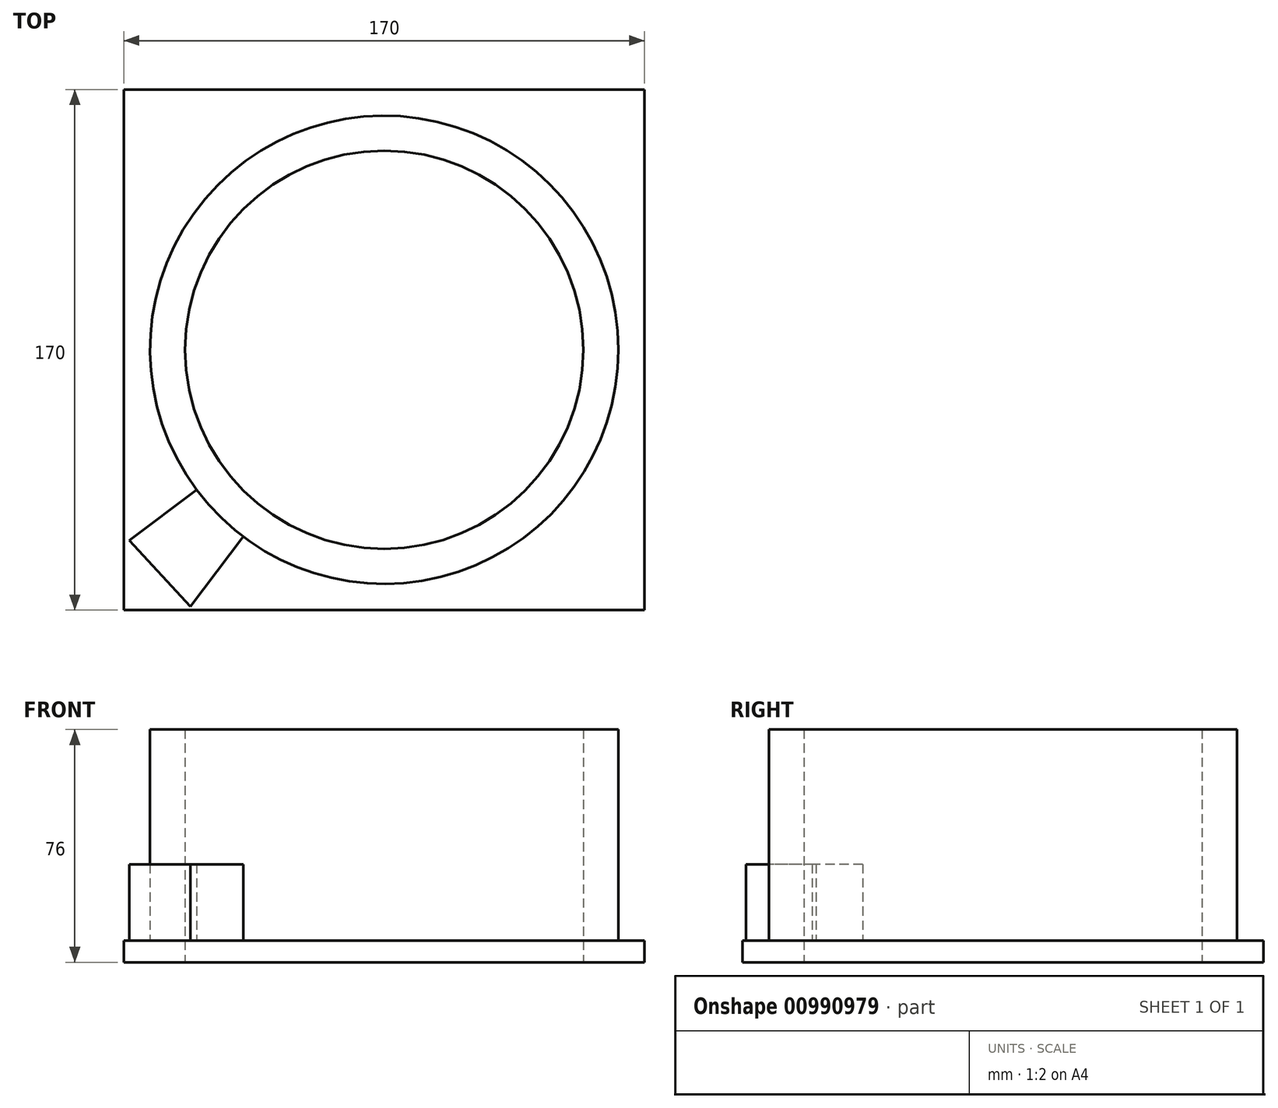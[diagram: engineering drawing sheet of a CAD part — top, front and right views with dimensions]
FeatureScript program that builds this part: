
annotation { "Feature Type Name" : "Feature", "Feature Type Description" : "" }
export const myFeature = defineFeature(function(context is Context, id is Id, definition is map)
    precondition{}
    {
        {
            var Q0;
            Q0=qCreatedBy(makeId("Top.planeOp"),FACE);
            var sketch = newSketch(context, id + "F0", { "sketchPlane" : qUnion([Q0])});
            skCircle(sketch, "E0", {"center": v(0, 0) * mm, "radius": 65 * mm});
            skLineSegment(sketch, "E1.bottom", {"start": v(85, -85) * mm, "end": v(-85, -85) * mm});
            skLineSegment(sketch, "E1.top", {"start": v(85, 85) * mm, "end": v(-85, 85) * mm});
            skLineSegment(sketch, "E1.left", {"start": v(85, -85) * mm, "end": v(85, 85) * mm});
            skLineSegment(sketch, "E1.right", {"start": v(-85, -85) * mm, "end": v(-85, 85) * mm});
            skPoint(sketch, "E2", {"position": v(-85, 0) * mm});
            skPoint(sketch, "E3", {"position": v(85, 0) * mm});
            skPoint(sketch, "E4", {"position": v(0, 85) * mm});
            skPoint(sketch, "E5", {"position": v(0, -85) * mm});
            skCircle(sketch, "E6", {"center": v(0, 0) * mm, "radius": 76.43 * mm});
            skSolve(sketch);
        }
        {
            var Q0;
            Q0=makeQuery(id+"F0.imprint","IMPRINT",FACE,{"disambiguationData":[TD([[makeQuery(id+"F0.imprint","IMPRINT",EDGE,{"derivedFrom":sQuery(id+"F0.wireOp",EDGE,"E0")}),-1.0]])]});
            extrude(context, id + "F1", {"entities" : qUnion([Q0]), "depth" : 69 * mm, "offsetDistance" : 25 * mm});
        }
        {
            var Q0;
            Q0=qSketchRegion(id+"F0",true);
            var Q1;
            Q1=makeQuery(id+"F0.imprint","IMPRINT",FACE,{"disambiguationData":[TD([[makeQuery(id+"F0.imprint","IMPRINT",EDGE,{"derivedFrom":sQuery(id+"F0.wireOp",EDGE,"E0")}),-1.0]])]});
            extrude(context, id + "F2", {"entities" : qUnion([Q0, Q1]), "operationType" : NewBodyOperationType.ADD, "oppositeDirection" : true, "depth" : 7 * mm, "offsetDistance" : 25 * mm});
        }
        {
            var Q0;
            Q0=makeQuery(id+"F0.imprint","IMPRINT",FACE,{"disambiguationData":[TD([[makeQuery(id+"F0.imprint","IMPRINT",EDGE,{"derivedFrom":sQuery(id+"F0.wireOp",EDGE,"E1.bottom")}),-1.0]])]});
            var sketch = newSketch(context, id + "F3", { "sketchPlane" : qUnion([Q0])});
            skLineSegment(sketch, "E7", {"start": v(-61.19, -45.8) * mm, "end": v(-83.2, -62.28) * mm});
            skLineSegment(sketch, "E8", {"start": v(-46.04, -61.01) * mm, "end": v(-63.3, -83.89) * mm});
            skLineSegment(sketch, "E9", {"start": v(-83.2, -62.28) * mm, "end": v(-63.3, -83.89) * mm});
            skSolve(sketch);
        }
        {
            var Q0;
            {var subQ0=sQuery(id+"F3.wireOp",EDGE,"E7");Q0=makeQuery(id+"F3.imprint","IMPRINT",FACE,{"disambiguationData":[TD([[makeQuery(id+"F3.imprint","IMPRINT",EDGE,{"derivedFrom":subQ0}),1.0]])]});}
            extrude(context, id + "F4", {"entities" : qUnion([Q0]), "operationType" : NewBodyOperationType.ADD, "depth" : 25 * mm, "offsetDistance" : 25 * mm});
        }
    });
